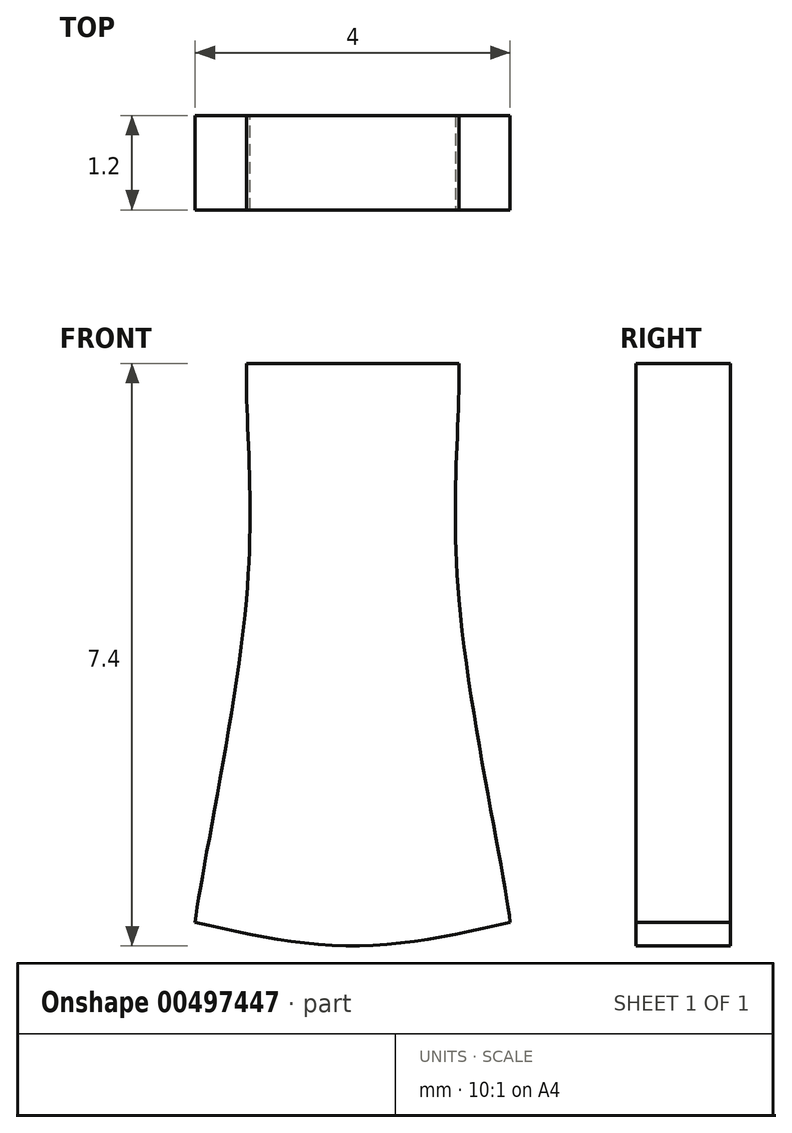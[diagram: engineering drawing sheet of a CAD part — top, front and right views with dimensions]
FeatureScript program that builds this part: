
annotation { "Feature Type Name" : "Feature", "Feature Type Description" : "" }
export const myFeature = defineFeature(function(context is Context, id is Id, definition is map)
    precondition{}
    {
        {
            var Q0;
            Q0=qCreatedBy(makeId("Front.planeOp"),FACE);
            var sketch = newSketch(context, id + "F0", { "sketchPlane" : qUnion([Q0])});
            skLineSegment(sketch, "E0", {"start": v(0, 0) * mm, "end": v(2.7, 0) * mm});
            skLineSegment(sketch, "E1", {"start": v(1.35, 0) * mm, "end": v(1.35, -3) * mm});
            skFitSpline(sketch, "E2", {"points": [v(0, 0) * mm, v(0, -3) * mm, v(-0.65, -7.1) * mm, v(-0.65, -7.4) * mm], "startDerivative": vector(-0.09, -6.5) * mm, "endDerivative": vector(0.15, -1.57) * mm});
            skFitSpline(sketch, "E3", {"points": [v(2.7, 0) * mm, v(2.7, -3) * mm, v(3.35, -7.1) * mm, v(3.35, -7.4) * mm], "startDerivative": vector(0.09, -6.5) * mm, "endDerivative": vector(-0.15, -1.57) * mm});
            skFitSpline(sketch, "E4", {"points": [v(-0.65, -7.1) * mm, v(1.35, -7.4) * mm, v(3.35, -7.1) * mm], "startDerivative": vector(4, -0.9) * mm, "endDerivative": vector(4, 0.9) * mm});
            skLineSegment(sketch, "E5", {"start": v(1.35, -3) * mm, "end": v(0, -3) * mm});
            skLineSegment(sketch, "E6", {"start": v(1.35, -3) * mm, "end": v(2.7, -3) * mm});
            skSolve(sketch);
        }
        {
            var Q0;
            Q0 = qSketchRegion(id + "F0", true);
            extrude(context, id + "F1", {"entities" : qUnion([Q0]), "depth" : 1.2 * mm});
        }
    });
